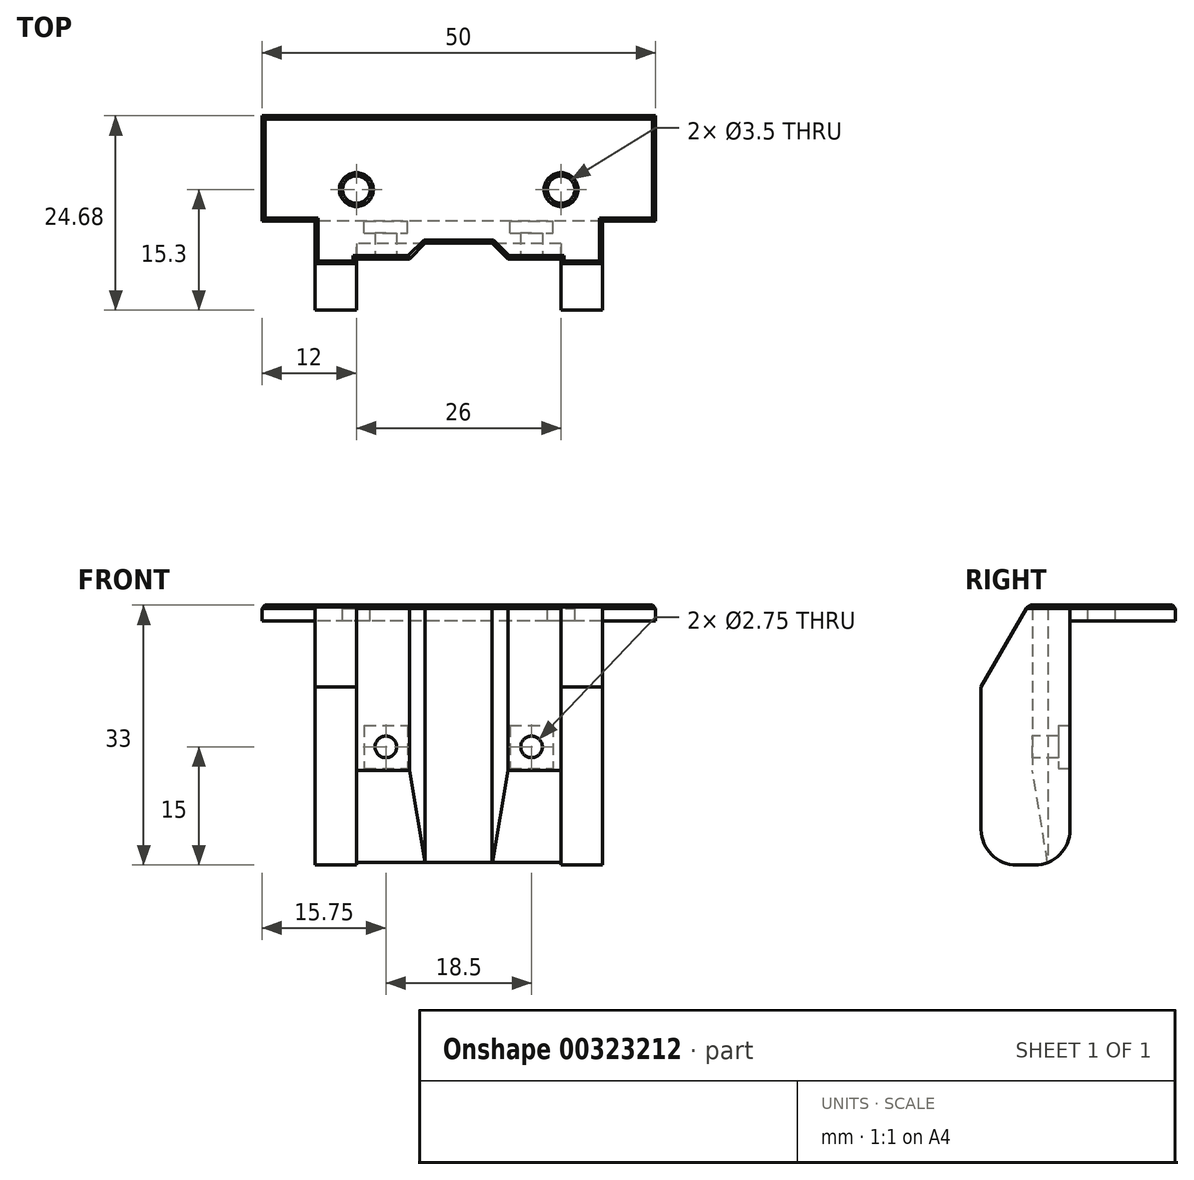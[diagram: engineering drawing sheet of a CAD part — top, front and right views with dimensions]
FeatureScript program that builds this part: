
annotation { "Feature Type Name" : "Feature", "Feature Type Description" : "" }
export const myFeature = defineFeature(function(context is Context, id is Id, definition is map)
    precondition{}
    {
        {
            var Q0;
            Q0=qCreatedBy(makeId("Right.planeOp"),FACE);
            var sketch = newSketch(context, id + "F0", { "sketchPlane" : qUnion([Q0])});
            skLineSegment(sketch, "E0", {"start": v(0, 0) * mm, "end": v(13.38, 0) * mm});
            skLineSegment(sketch, "E1", {"start": v(13.38, 0) * mm, "end": v(13.38, 2) * mm});
            skLineSegment(sketch, "E2", {"start": v(13.38, 2) * mm, "end": v(0, 2) * mm});
            skLineSegment(sketch, "E3", {"start": v(0, 2) * mm, "end": v(0, 0) * mm});
            skSolve(sketch);
        }
        {
            var Q0;
            Q0=makeQuery(id+"F0.imprint","IMPRINT",FACE,{"disambiguationData":[TD([[makeQuery(id+"F0.imprint","IMPRINT",EDGE,{"derivedFrom":sQuery(id+"F0.wireOp",EDGE,"E0")}),1.0]])]});
            extrude(context, id + "F1", {"entities" : qUnion([Q0]), "endBound" : BoundingType.SYMMETRIC, "depth" : 50 * mm});
        }
        {
            var Q0;
            Q0=makeQuery(id+"F1.opExtrude","SWEPT_FACE",FACE,{"disambiguationData":[OSD([sQuery(id+"F0.wireOp",EDGE,"E2")])]});
            var sketch = newSketch(context, id + "F2", { "sketchPlane" : qUnion([Q0])});
            skLineSegment(sketch, "E4", {"start": v(-25, 4) * mm, "end": v(25, 4) * mm, "construction": true});
            skLineSegment(sketch, "E5", {"start": v(0, 13.38) * mm, "end": v(0, 0) * mm, "construction": true});
            skCircle(sketch, "E6", {"center": v(-13, 4) * mm, "radius": 1.75 * mm});
            skCircle(sketch, "E7", {"center": v(13, 4) * mm, "radius": 1.75 * mm});
            skSolve(sketch);
        }
        {
            var Q0;
            Q0=qSketchRegion(id+"F2",true);
            extrude(context, id + "F3", {"entities" : qUnion([Q0]), "operationType" : NewBodyOperationType.REMOVE, "endBound" : BoundingType.UP_TO_NEXT, "oppositeDirection" : true, "depth" : 25 * mm});
        }
        {
            var Q0;
            Q0=qCreatedBy(makeId("Right.planeOp"),FACE);
            var sketch = newSketch(context, id + "F4", { "sketchPlane" : qUnion([Q0])});
            skLineSegment(sketch, "E8.bottom", {"start": v(0, 2) * mm, "end": v(-11.3, 2) * mm});
            skLineSegment(sketch, "E8.top", {"start": v(0, -31) * mm, "end": v(-11.3, -31) * mm});
            skLineSegment(sketch, "E8.left", {"start": v(0, 2) * mm, "end": v(0, -31) * mm});
            skLineSegment(sketch, "E8.right", {"start": v(-11.3, 2) * mm, "end": v(-11.3, -31) * mm});
            skSolve(sketch);
        }
        {
            var Q0;
            Q0=qSketchRegion(id+"F4",true);
            extrude(context, id + "F5", {"entities" : qUnion([Q0]), "operationType" : NewBodyOperationType.ADD, "endBound" : BoundingType.SYMMETRIC, "depth" : 36.5 * mm});
        }
        {
            var Q0;
            Q0=makeQuery(id+"F5.opExtrude","SWEPT_FACE",FACE,{"disambiguationData":[OSD([sQuery(id+"F4.wireOp",EDGE,"E8.top")])]});
            var sketch = newSketch(context, id + "F6", { "sketchPlane" : qUnion([Q0])});
            skLineSegment(sketch, "E9.bottom", {"start": v(-13, 11.3) * mm, "end": v(13, 11.3) * mm});
            skLineSegment(sketch, "E9.top", {"start": v(-13, 4.8) * mm, "end": v(13, 4.8) * mm});
            skLineSegment(sketch, "E9.left", {"start": v(-13, 11.3) * mm, "end": v(-13, 4.8) * mm});
            skLineSegment(sketch, "E9.right", {"start": v(13, 11.3) * mm, "end": v(13, 4.8) * mm});
            skLineSegment(sketch, "E10", {"start": v(0, 11.3) * mm, "end": v(0, 0) * mm, "construction": true});
            skSolve(sketch);
        }
        {
            var Q0;
            Q0=qSketchRegion(id+"F6",true);
            extrude(context, id + "F7", {"entities" : qUnion([Q0]), "operationType" : NewBodyOperationType.REMOVE, "endBound" : BoundingType.UP_TO_NEXT, "oppositeDirection" : true, "depth" : 25 * mm});
        }
        {
            var Q0;
            Q0=makeQuery(id+"F5.opExtrude","SWEPT_FACE",FACE,{"disambiguationData":[OSD([sQuery(id+"F4.wireOp",EDGE,"E8.top")])]});
            var sketch = newSketch(context, id + "F8", { "sketchPlane" : qUnion([Q0])});
            skLineSegment(sketch, "E11", {"start": v(0, 4.8) * mm, "end": v(0, 0) * mm, "construction": true});
            skLineSegment(sketch, "E12", {"start": v(-6.25, 4.8) * mm, "end": v(-4.25, 2.8) * mm});
            skLineSegment(sketch, "E13", {"start": v(-4.25, 2.8) * mm, "end": v(4.25, 2.8) * mm});
            skLineSegment(sketch, "E14", {"start": v(4.25, 2.8) * mm, "end": v(6.25, 4.8) * mm});
            skLineSegment(sketch, "E15", {"start": v(6.25, 4.8) * mm, "end": v(-6.25, 4.8) * mm});
            skSolve(sketch);
        }
        {
            var Q0;
            Q0=qSketchRegion(id+"F8",true);
            extrude(context, id + "F9", {"entities" : qUnion([Q0]), "operationType" : NewBodyOperationType.REMOVE, "endBound" : BoundingType.UP_TO_NEXT, "oppositeDirection" : true, "depth" : 25 * mm});
        }
        {
            var Q0;
            Q0=qCreatedBy(makeId("Right.planeOp"),FACE);
            var sketch = newSketch(context, id + "F10", { "sketchPlane" : qUnion([Q0])});
            skLineSegment(sketch, "E16", {"start": v(-2.8, -31) * mm, "end": v(-4.8, -19) * mm});
            skLineSegment(sketch, "E17", {"start": v(-4.8, -19) * mm, "end": v(-4.8, -31) * mm});
            skLineSegment(sketch, "E18", {"start": v(-4.8, -31) * mm, "end": v(-2.8, -31) * mm});
            skSolve(sketch);
        }
        {
            var Q0;
            Q0=qSketchRegion(id+"F10",true);
            var Q1;
            Q1=makeQuery(id+"F7.boolean.opBoolean","COPY",FACE,{"derivedFrom":makeQuery(id+"F7.opExtrude","SWEPT_FACE",FACE,{"disambiguationData":[OSD([sQuery(id+"F6.wireOp",EDGE,"E9.right")])]})});
            var Q2;
            Q2=makeQuery(id+"F7.boolean.opBoolean","COPY",FACE,{"derivedFrom":makeQuery(id+"F7.opExtrude","SWEPT_FACE",FACE,{"disambiguationData":[OSD([sQuery(id+"F6.wireOp",EDGE,"E9.left")])]})});
            extrude(context, id + "F11", {"entities" : qUnion([Q0]), "operationType" : NewBodyOperationType.REMOVE, "endBound" : BoundingType.UP_TO_SURFACE, "endBoundEntityFace" : qUnion([Q1]), "depth" : 25 * mm, "hasSecondDirection" : true, "secondDirectionBound" : SecondDirectionBoundingType.UP_TO_SURFACE, "secondDirectionOppositeDirection" : true, "secondDirectionBoundEntityFace" : qUnion([Q2]), "secondDirectionDepth" : 25 * mm});
        }
        {
            var Q0;
            Q0=makeQuery(id+"F9.boolean.opBoolean","SPLIT",FACE,{"disambiguationData":[TD([makeQuery(id+"F7.boolean.opBoolean","COPY",FACE,{"derivedFrom":makeQuery(id+"F7.opExtrude","SWEPT_FACE",FACE,{"disambiguationData":[OSD([sQuery(id+"F6.wireOp",EDGE,"E9.left")])]})})])],"derivedFrom":makeQuery(id+"F7.boolean.opBoolean","COPY",FACE,{"derivedFrom":makeQuery(id+"F7.opExtrude","SWEPT_FACE",FACE,{"disambiguationData":[OSD([sQuery(id+"F6.wireOp",EDGE,"E9.top")])]})})});
            var sketch = newSketch(context, id + "F12", { "sketchPlane" : qUnion([Q0])});
            skCircle(sketch, "E19", {"center": v(-9.25, -16) * mm, "radius": 1.38 * mm});
            skLineSegment(sketch, "E20", {"start": v(0, 2) * mm, "end": v(0, -31) * mm, "construction": true});
            skCircle(sketch, "E21.MirrorC", {"center": v(9.25, -16) * mm, "radius": 1.38 * mm});
            skSolve(sketch);
        }
        {
            var Q0;
            Q0=qSketchRegion(id+"F12",true);
            extrude(context, id + "F13", {"entities" : qUnion([Q0]), "operationType" : NewBodyOperationType.REMOVE, "endBound" : BoundingType.UP_TO_NEXT, "oppositeDirection" : true, "depth" : 25 * mm});
        }
        {
            var Q0;
            Q0=makeQuery(id+"F5.opExtrude","SWEPT_FACE",FACE,{"disambiguationData":[OSD([sQuery(id+"F4.wireOp",EDGE,"E8.left")])]});
            var sketch = newSketch(context, id + "F14", { "sketchPlane" : qUnion([Q0])});
            skLineSegment(sketch, "E22.bottom", {"start": v(-6.5, -13.25) * mm, "end": v(-12, -13.25) * mm});
            skLineSegment(sketch, "E22.top", {"start": v(-6.5, -18.75) * mm, "end": v(-12, -18.75) * mm});
            skLineSegment(sketch, "E22.left", {"start": v(-6.5, -13.25) * mm, "end": v(-6.5, -18.75) * mm});
            skLineSegment(sketch, "E22.right", {"start": v(-12, -13.25) * mm, "end": v(-12, -18.75) * mm});
            skPoint(sketch, "E22.middle", {"position": v(-9.25, -16) * mm});
            skLineSegment(sketch, "E23.bottom", {"start": v(12, -13.25) * mm, "end": v(6.5, -13.25) * mm});
            skLineSegment(sketch, "E23.top", {"start": v(12, -18.75) * mm, "end": v(6.5, -18.75) * mm});
            skLineSegment(sketch, "E23.left", {"start": v(12, -13.25) * mm, "end": v(12, -18.75) * mm});
            skLineSegment(sketch, "E23.right", {"start": v(6.5, -13.25) * mm, "end": v(6.5, -18.75) * mm});
            skPoint(sketch, "E23.middle", {"position": v(9.25, -16) * mm});
            skSolve(sketch);
        }
        {
            var Q0;
            Q0=qSketchRegion(id+"F14",true);
            extrude(context, id + "F15", {"entities" : qUnion([Q0]), "operationType" : NewBodyOperationType.REMOVE, "oppositeDirection" : true, "depth" : 1.5 * mm});
        }
        {
            var Q0;
            {var subQ0=sQuery(id+"F4.wireOp",EDGE,"E8.right");var subQ1=sQuery(id+"F4.wireOp",EDGE,"E8.top");Q0=makeQuery(id+"F7.boolean.opBoolean","SPLIT",EDGE,{"disambiguationData":[TD([makeQuery(id+"F7.opExtrude","SWEPT_FACE",FACE,{"disambiguationData":[OSD([sQuery(id+"F6.wireOp",EDGE,"E9.left")])]})])],"derivedFrom":makeQuery(id+"F5.opExtrude","SWEPT_EDGE",EDGE,{"disambiguationData":[OSD([subQ1,subQ0])]})});}
            var Q1;
            {var subQ0=sQuery(id+"F4.wireOp",EDGE,"E8.right");var subQ1=sQuery(id+"F4.wireOp",EDGE,"E8.top");Q1=makeQuery(id+"F7.boolean.opBoolean","SPLIT",EDGE,{"disambiguationData":[TD([makeQuery(id+"F7.opExtrude","SWEPT_FACE",FACE,{"disambiguationData":[OSD([sQuery(id+"F6.wireOp",EDGE,"E9.right")])]})])],"derivedFrom":makeQuery(id+"F5.opExtrude","SWEPT_EDGE",EDGE,{"disambiguationData":[OSD([subQ1,subQ0])]})});}
            var Q2;
            Q2=makeQuery(id+"F5.opExtrude","SWEPT_EDGE",EDGE,{"disambiguationData":[OSD([sQuery(id+"F4.wireOp",EDGE,"E8.top"),sQuery(id+"F4.wireOp",EDGE,"E8.left")])]});
            fillet(context, id + "F16", {"entities" : qUnion([Q0, Q1, Q2]), "radius" : 4.5 * mm, "tangentPropagation" : true, "allowEdgeOverflow" : false});
        }
        {
            var Q0;
            {var subQ0=sQuery(id+"F4.wireOp",EDGE,"E8.right");var subQ1=sQuery(id+"F4.wireOp",EDGE,"E8.bottom");Q0=makeQuery(id+"F7.boolean.opBoolean","SPLIT",EDGE,{"disambiguationData":[TD([makeQuery(id+"F7.opExtrude","SWEPT_FACE",FACE,{"disambiguationData":[OSD([sQuery(id+"F6.wireOp",EDGE,"E9.left")])]})])],"derivedFrom":makeQuery(id+"F5.opExtrude","SWEPT_EDGE",EDGE,{"disambiguationData":[OSD([subQ1,subQ0])]})});}
            var Q1;
            {var subQ0=sQuery(id+"F4.wireOp",EDGE,"E8.right");var subQ1=sQuery(id+"F4.wireOp",EDGE,"E8.bottom");Q1=makeQuery(id+"F7.boolean.opBoolean","SPLIT",EDGE,{"disambiguationData":[TD([makeQuery(id+"F7.opExtrude","SWEPT_FACE",FACE,{"disambiguationData":[OSD([sQuery(id+"F6.wireOp",EDGE,"E9.right")])]})])],"derivedFrom":makeQuery(id+"F5.opExtrude","SWEPT_EDGE",EDGE,{"disambiguationData":[OSD([subQ1,subQ0])]})});}
            chamfer(context, id + "F17", {"entities" : qUnion([Q0, Q1]), "chamferType" : ChamferType.OFFSET_ANGLE, "width" : 6 * mm, "oppositeDirection" : true, "angle" : 60 * degree, "tangentPropagation" : true});
        }
        {
            var Q0;
            Q0=makeQuery(id+"F5.boolean.opBoolean","MERGE",FACE,{"derivedFrom":[makeQuery(id+"F1.opExtrude","SWEPT_FACE",FACE,{"disambiguationData":[OSD([sQuery(id+"F0.wireOp",EDGE,"E2")])]}),makeQuery(id+"F5.opExtrude","SWEPT_FACE",FACE,{"disambiguationData":[OSD([sQuery(id+"F4.wireOp",EDGE,"E8.bottom")])]})]});
            chamfer(context, id + "F18", {"entities" : qUnion([Q0]), "width" : 0.4 * mm, "tangentPropagation" : true});
        }
    });
